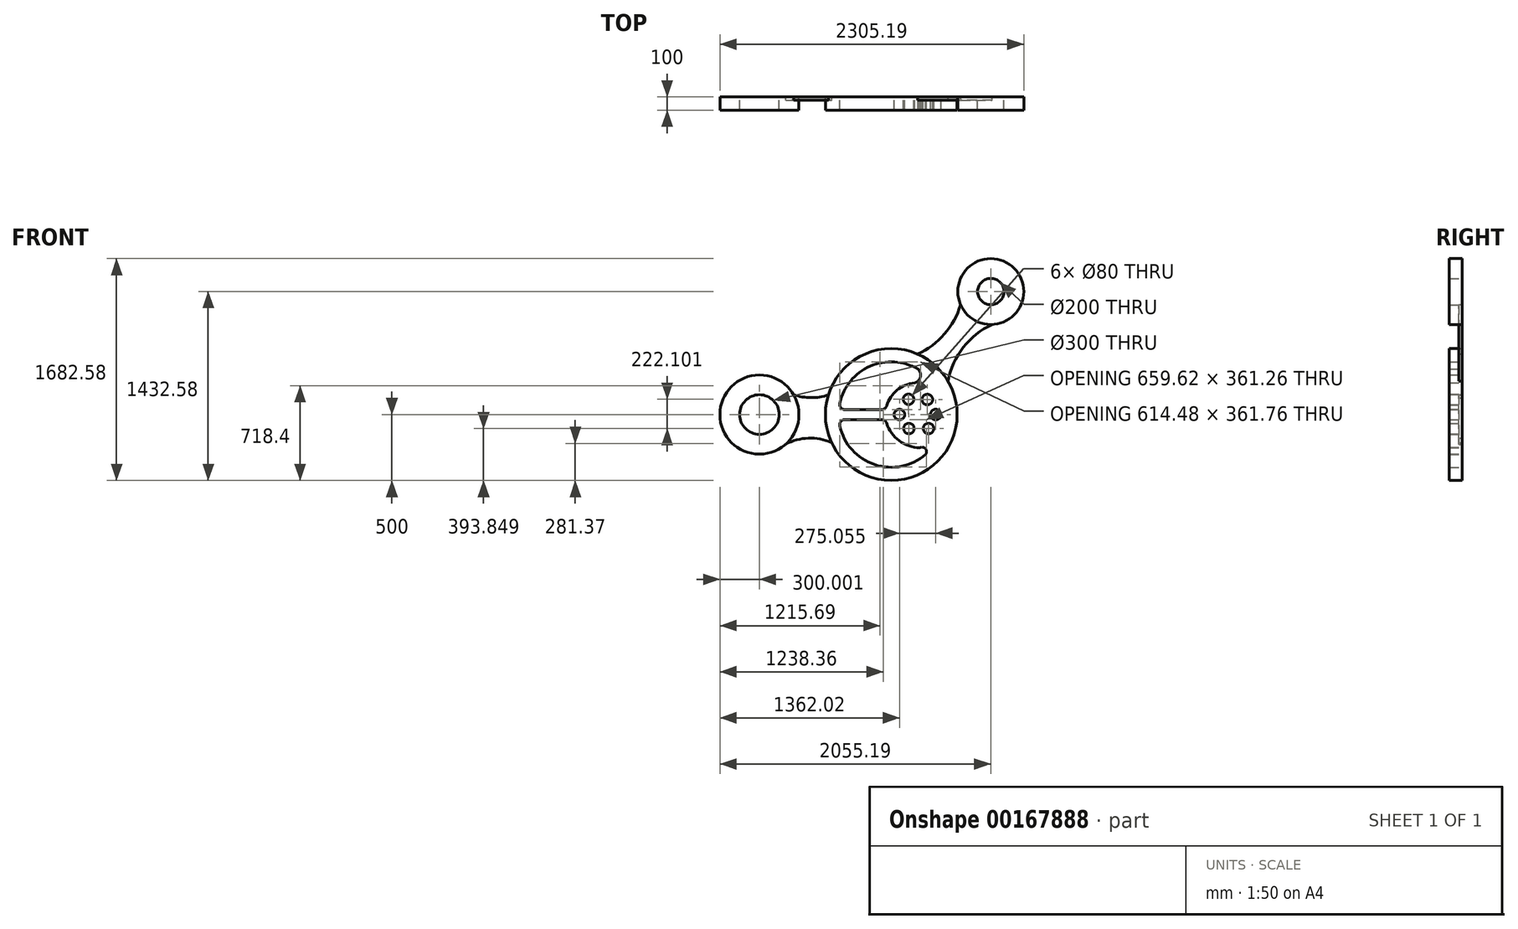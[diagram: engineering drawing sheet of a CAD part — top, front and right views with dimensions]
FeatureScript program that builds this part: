
annotation { "Feature Type Name" : "Feature", "Feature Type Description" : "" }
export const myFeature = defineFeature(function(context is Context, id is Id, definition is map)
    precondition{}
    {
        {
            var Q0;
            Q0=qCreatedBy(makeId("Front.planeOp"),FACE);
            var sketch = newSketch(context, id + "F0", { "sketchPlane" : qUnion([Q0])});
            skArc(sketch, "E0", {"start": v(-698.26, 150.18) * mm, "mid": v(-1254.03, 48.39) * mm, "end": v(-759.58, -225.04) * mm});
            skArc(sketch, "E1", {"start": v(808.27, 682.82) * mm, "mid": v(929.7, 1144.6) * mm, "end": v(567.91, 833) * mm});
            skArc(sketch, "E2", {"start": v(241.82, 458.36) * mm, "mid": v(-165.32, 454.97) * mm, "end": v(-434.96, 149.9) * mm});
            skArc(sketch, "E3", {"start": v(-410.08, -213.52) * mm, "mid": v(-586.15, -179.07) * mm, "end": v(-759.58, -225.04) * mm});
            skArc(sketch, "E4", {"start": v(-698.26, 150.18) * mm, "mid": v(-566.63, 127.75) * mm, "end": v(-434.96, 149.9) * mm});
            skArc(sketch, "E5", {"start": v(808.27, 682.82) * mm, "mid": v(588.97, 509) * mm, "end": v(472.35, 254.63) * mm});
            skArc(sketch, "E6", {"start": v(241.82, 458.36) * mm, "mid": v(445.45, 610.35) * mm, "end": v(567.91, 833) * mm});
            skArc(sketch, "E7", {"start": v(244.7, 344.86) * mm, "mid": v(-117.86, 366.65) * mm, "end": v(-348.58, 86.13) * mm});
            skCircle(sketch, "E8", {"center": v(379.12, 0) * mm, "radius": 40 * mm});
            skCircle(sketch, "E9", {"center": v(104.06, 0) * mm, "radius": 40 * mm});
            skCircle(sketch, "E10", {"center": v(315.88, 113.73) * mm, "radius": 40 * mm});
            skCircle(sketch, "E11", {"center": v(173.74, 115.95) * mm, "radius": 40 * mm});
            skCircle(sketch, "E12", {"center": v(324.76, -106.15) * mm, "radius": 40 * mm});
            skCircle(sketch, "E13", {"center": v(175.96, -106.15) * mm, "radius": 40 * mm});
            skLineSegment(sketch, "E14", {"start": v(-309.51, 37.52) * mm, "end": v(-31.53, 37.52) * mm});
            skLineSegment(sketch, "E15", {"start": v(-309.4, -38) * mm, "end": v(-30.6, -38) * mm});
            skArc(sketch, "E16", {"start": v(7.43, -65.57) * mm, "mid": v(102.99, -198.34) * mm, "end": v(257.67, -251.57) * mm});
            skArc(sketch, "E17", {"start": v(218.78, 239.4) * mm, "mid": v(86.32, 185.03) * mm, "end": v(6.76, 65.97) * mm});
            skArc(sketch, "E18", {"start": v(303.98, -302.3) * mm, "mid": v(301.08, -258.45) * mm, "end": v(257.67, -251.57) * mm});
            skArc(sketch, "E19", {"start": v(218.78, 239.4) * mm, "mid": v(263.21, 284.4) * mm, "end": v(244.7, 344.86) * mm});
            skPoint(sketch, "E20.orphan", {"position": v(218.78, 358.84) * mm});
            skArc(sketch, "E21.trimOffspring", {"start": v(-348.46, -86.67) * mm, "mid": v(-83.48, -379.8) * mm, "end": v(303.98, -302.3) * mm});
            skPoint(sketch, "E22.visualSharp", {"position": v(-356.2, 37.52) * mm});
            skArc(sketch, "E22.filletArc", {"start": v(-348.58, 86.13) * mm, "mid": v(-340.7, 52.46) * mm, "end": v(-309.51, 37.52) * mm});
            skPoint(sketch, "E23.visualSharp", {"position": v(0, 37.52) * mm});
            skArc(sketch, "E23.filletArc", {"start": v(-31.53, 37.52) * mm, "mid": v(-7.68, 45.4) * mm, "end": v(6.76, 65.97) * mm});
            skPoint(sketch, "E24.visualSharp", {"position": v(-356.15, -38) * mm});
            skArc(sketch, "E24.filletArc", {"start": v(-309.4, -38) * mm, "mid": v(-340.6, -52.97) * mm, "end": v(-348.46, -86.67) * mm});
            skPoint(sketch, "E25.visualSharp", {"position": v(0, -38) * mm});
            skArc(sketch, "E25.filletArc", {"start": v(7.43, -65.57) * mm, "mid": v(-7.11, -45.62) * mm, "end": v(-30.6, -38) * mm});
            skCircle(sketch, "E26", {"center": v(-957.96, 0) * mm, "radius": 150 * mm});
            skCircle(sketch, "E27", {"center": v(797.23, 932.58) * mm, "radius": 100 * mm});
            skPoint(sketch, "E28.start.orphan", {"position": v(-1092.85, 0) * mm});
            skArc(sketch, "E29.trimOffspring", {"start": v(-410.08, -213.52) * mm, "mid": v(276.37, -441.69) * mm, "end": v(472.35, 254.63) * mm});
            skPoint(sketch, "E30.center.orphan", {"position": v(242.04, 0) * mm});
            skCircle(sketch, "E31", {"center": v(-957.96, 0) * mm, "radius": 300 * mm});
            skCircle(sketch, "E32", {"center": v(797.23, 932.58) * mm, "radius": 250 * mm});
            skCircle(sketch, "E33", {"center": v(42.04, 0) * mm, "radius": 500 * mm});
            skSolve(sketch);
        }
        {
            var Q0;
            Q0=makeQuery(id+"F0.imprint","IMPRINT",FACE,{"disambiguationData":[TD([[makeQuery(id+"F0.imprint","IMPRINT",EDGE,{"derivedFrom":sQuery(id+"F0.wireOp",EDGE,"E27")}),-1.0]])]});
            var Q1;
            Q1=makeQuery(id+"F0.imprint","IMPRINT",FACE,{"disambiguationData":[TD([[makeQuery(id+"F0.imprint","IMPRINT",EDGE,{"derivedFrom":sQuery(id+"F0.wireOp",EDGE,"E7")}),-1.0]])]});
            var Q2;
            Q2=makeQuery(id+"F0.imprint","IMPRINT",FACE,{"disambiguationData":[TD([[makeQuery(id+"F0.imprint","IMPRINT",EDGE,{"derivedFrom":sQuery(id+"F0.wireOp",EDGE,"E26")}),-1.0]])]});
            extrude(context, id + "F1", {"entities" : qUnion([Q0, Q1, Q2]), "depth" : 100 * mm});
        }
        {
            var Q0;
            {var subQ0=sQuery(id+"F0.wireOp",EDGE,"E3");Q0=makeQuery(id+"F0.imprint","IMPRINT",FACE,{"disambiguationData":[TD([[makeQuery(id+"F0.imprint","IMPRINT",EDGE,{"derivedFrom":subQ0}),-1.0]])]});}
            var Q1;
            {var subQ0=sQuery(id+"F0.wireOp",EDGE,"E5");Q1=makeQuery(id+"F0.imprint","IMPRINT",FACE,{"disambiguationData":[TD([[makeQuery(id+"F0.imprint","IMPRINT",EDGE,{"derivedFrom":subQ0}),-1.0]])]});}
            extrude(context, id + "F2", {"entities" : qUnion([Q0, Q1]), "depth" : 25 * mm});
        }
    });
